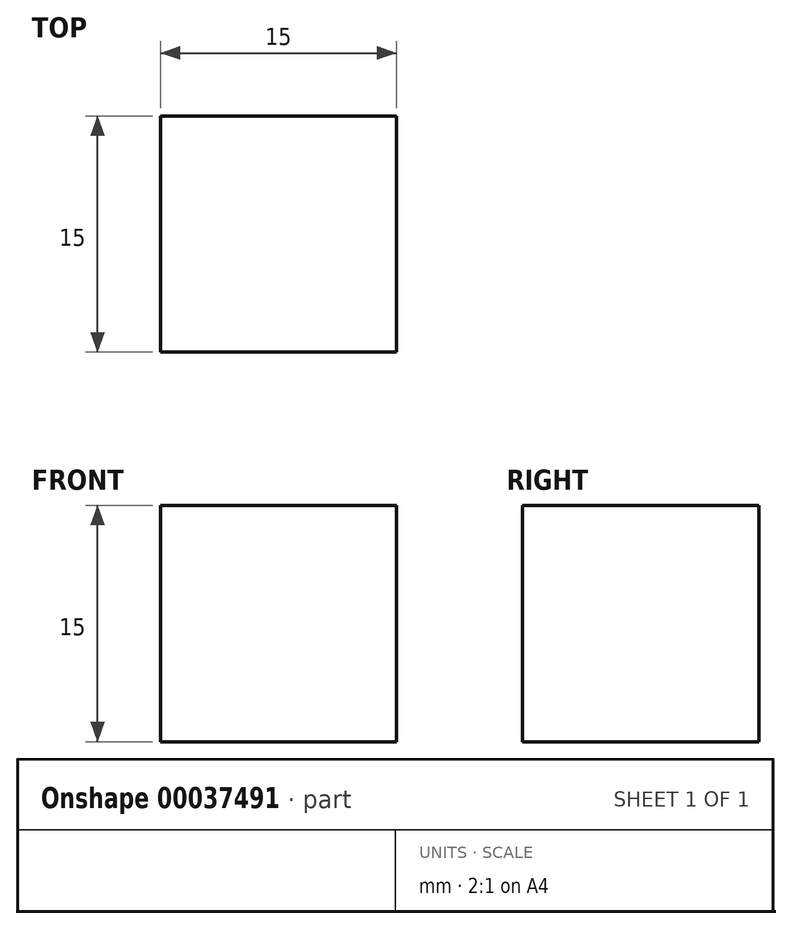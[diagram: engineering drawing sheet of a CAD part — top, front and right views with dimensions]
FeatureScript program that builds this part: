
annotation { "Feature Type Name" : "Feature", "Feature Type Description" : "" }
export const myFeature = defineFeature(function(context is Context, id is Id, definition is map)
    precondition{}
    {
        {
            var Q0;
            Q0=qCreatedBy(makeId("Top.planeOp"),FACE);
            var sketch = newSketch(context, id + "F0", { "sketchPlane" : qUnion([Q0])});
            skLineSegment(sketch, "E0.bottom", {"start": v(7.5, -7.5) * mm, "end": v(-7.5, -7.5) * mm});
            skLineSegment(sketch, "E0.top", {"start": v(7.5, 7.5) * mm, "end": v(-7.5, 7.5) * mm});
            skLineSegment(sketch, "E0.left", {"start": v(7.5, -7.5) * mm, "end": v(7.5, 7.5) * mm});
            skLineSegment(sketch, "E0.right", {"start": v(-7.5, -7.5) * mm, "end": v(-7.5, 7.5) * mm});
            skPoint(sketch, "E0.middle", {"position": v(0, 0) * mm});
            skSolve(sketch);
        }
        {
            var Q0;
            Q0=makeQuery(id+"F0.imprint","IMPRINT",FACE,{"disambiguationData":[TD([[makeQuery(id+"F0.imprint","IMPRINT",EDGE,{"derivedFrom":sQuery(id+"F0.wireOp",EDGE,"E0.bottom")}),-1.0]])]});
            extrude(context, id + "F1", {"entities" : qUnion([Q0]), "oppositeDirection" : true, "depth" : 15 * mm});
        }
    });
